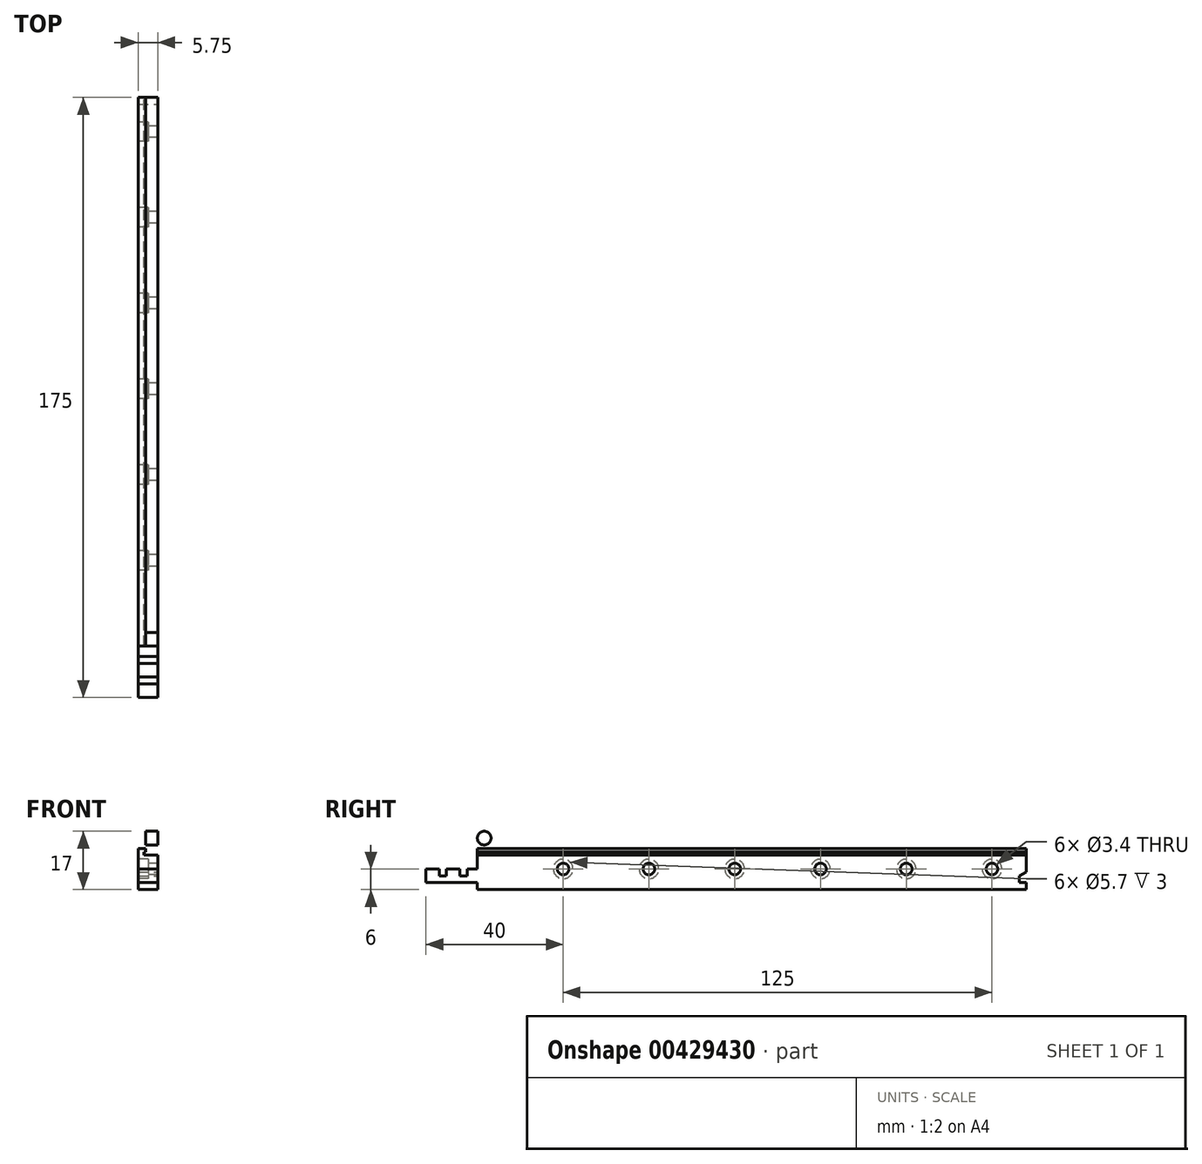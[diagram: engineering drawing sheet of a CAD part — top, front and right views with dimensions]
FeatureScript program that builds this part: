
annotation { "Feature Type Name" : "Feature", "Feature Type Description" : "" }
export const myFeature = defineFeature(function(context is Context, id is Id, definition is map)
    precondition{}
    {
        {
            var Q0;
            Q0=qCreatedBy(makeId("Right.planeOp"),FACE);
            var sketch = newSketch(context, id + "F0", { "sketchPlane" : qUnion([Q0])});
            skLineSegment(sketch, "E0.bottom", {"start": v(-160, 10) * mm, "end": v(0, 10) * mm});
            skLineSegment(sketch, "E0.top", {"start": v(-160, 0) * mm, "end": v(0, 0) * mm});
            skLineSegment(sketch, "E0.left", {"start": v(-160, 10) * mm, "end": v(-160, 0) * mm});
            skLineSegment(sketch, "E0.right", {"start": v(0, 10) * mm, "end": v(0, 0) * mm});
            skLineSegment(sketch, "E1.bottom", {"start": v(-160, 10) * mm, "end": v(-156, 10) * mm});
            skLineSegment(sketch, "E1.top", {"start": v(-158, 15) * mm, "end": v(-158, 15) * mm});
            skLineSegment(sketch, "E1.left", {"start": v(-160, 10) * mm, "end": v(-160, 13) * mm});
            skLineSegment(sketch, "E1.right", {"start": v(-156, 10) * mm, "end": v(-156, 13) * mm});
            skPoint(sketch, "E2.visualSharp", {"position": v(-160, 15) * mm});
            skArc(sketch, "E2.filletArc", {"start": v(-158, 15) * mm, "mid": v(-159.41, 14.41) * mm, "end": v(-160, 13) * mm});
            skPoint(sketch, "E3.visualSharp", {"position": v(-156, 15) * mm});
            skArc(sketch, "E3.filletArc", {"start": v(-156, 13) * mm, "mid": v(-156.59, 14.41) * mm, "end": v(-158, 15) * mm});
            skSolve(sketch);
        }
        {
            var Q0;
            Q0=makeQuery(id+"F0.imprint","IMPRINT",FACE,{"disambiguationData":[TD([[makeQuery(id+"F0.imprint","IMPRINT",EDGE,{"derivedFrom":sQuery(id+"F0.wireOp",EDGE,"E0.bottom")}),-1.0]])]});
            var Q1;
            Q1=makeQuery(id+"F0.imprint","IMPRINT",FACE,{"disambiguationData":[TD([[makeQuery(id+"F0.imprint","IMPRINT",EDGE,{"derivedFrom":sQuery(id+"F0.wireOp",EDGE,"E1.bottom")}),1.0]])]});
            extrude(context, id + "F1", {"entities" : qUnion([Q0, Q1]), "depth" : 5.75 * mm});
        }
        {
            var Q0;
            Q0=makeQuery(id+"F1.opExtrude","CAP_FACE",FACE,{"disambiguationData":[OSD([sQuery(id+"F0.wireOp",EDGE,"E0.bottom"),sQuery(id+"F0.wireOp",EDGE,"E0.top"),sQuery(id+"F0.wireOp",EDGE,"E0.left"),sQuery(id+"F0.wireOp",EDGE,"E0.right")])],"isStart":false});
            var sketch = newSketch(context, id + "F2", { "sketchPlane" : qUnion([Q0])});
            skLineSegment(sketch, "E4.bottom", {"start": v(-160, 9) * mm, "end": v(0, 9) * mm});
            skLineSegment(sketch, "E4.top", {"start": v(-160, 8.1) * mm, "end": v(0, 8.1) * mm});
            skLineSegment(sketch, "E4.left", {"start": v(-160, 9) * mm, "end": v(-160, 8.1) * mm});
            skLineSegment(sketch, "E4.right", {"start": v(0, 9) * mm, "end": v(0, 8.1) * mm});
            skSolve(sketch);
        }
        {
            var Q0;
            Q0=makeQuery(id+"F2.imprint","IMPRINT",FACE,{"disambiguationData":[TD([[makeQuery(id+"F2.imprint","IMPRINT",EDGE,{"derivedFrom":sQuery(id+"F2.wireOp",EDGE,"E4.bottom")}),-1.0]])]});
            extrude(context, id + "F3", {"entities" : qUnion([Q0]), "operationType" : NewBodyOperationType.REMOVE, "oppositeDirection" : true, "depth" : 4.1 * mm});
        }
        {
            var Q0;
            {var subQ0=sQuery(id+"F0.wireOp",EDGE,"E0.bottom");var subQ1=sQuery(id+"F0.wireOp",EDGE,"E0.right");var subQ2=sQuery(id+"F0.wireOp",EDGE,"E0.left");Q0=makeQuery(id+"F3.boolean.opBoolean","SPLIT",FACE,{"disambiguationData":[TD([makeQuery(id+"F1.opExtrude","SWEPT_FACE",FACE,{"disambiguationData":[OSD([subQ0])]})])],"derivedFrom":makeQuery(id+"F1.opExtrude","CAP_FACE",FACE,{"disambiguationData":[OSD([subQ0,sQuery(id+"F0.wireOp",EDGE,"E0.top"),subQ2,subQ1])],"isStart":false})});}
            var sketch = newSketch(context, id + "F4", { "sketchPlane" : qUnion([Q0])});
            skSolve(sketch);
        }
        {
            var Q0;
            Q0 = qSketchRegion(id + "F4", true);
            var Q1;
            {var subQ0=sQuery(id+"F0.wireOp",EDGE,"E0.bottom");Q1=makeQuery(id+"F4.imprint","IMPRINT",FACE,{"disambiguationData":[TD([[makeQuery(id+"F4.imprint","IMPRINT",EDGE,{"derivedFrom":makeQuery(id+"F1.opExtrude","CAP_EDGE",EDGE,{"disambiguationData":[OSD([subQ0])],"isStart":false})}),-1.0]])]});}
            extrude(context, id + "F5", {"entities" : qUnion([Q0, Q1]), "operationType" : NewBodyOperationType.REMOVE, "oppositeDirection" : true, "depth" : 3.5 * mm});
        }
        {
            var Q0;
            Q0=makeQuery(id+"F1.opExtrude","CAP_FACE",FACE,{"disambiguationData":[OSD([sQuery(id+"F0.wireOp",EDGE,"E0.bottom"),sQuery(id+"F0.wireOp",EDGE,"E0.top"),sQuery(id+"F0.wireOp",EDGE,"E0.left"),sQuery(id+"F0.wireOp",EDGE,"E0.right")])],"isStart":true});
            var sketch = newSketch(context, id + "F6", { "sketchPlane" : qUnion([Q0])});
            skLineSegment(sketch, "E5", {"start": v(0, 4) * mm, "end": v(160, 4) * mm, "construction": true});
            skPoint(sketch, "E5.endSnap0", {"position": v(160, 6.5) * mm});
            skCircle(sketch, "E6", {"center": v(135, 4) * mm, "radius": 1.7 * mm});
            skCircle(sketch, "E7", {"center": v(3, 4) * mm, "radius": 1.25 * mm});
            skCircle(sketch, "E8.1.0.0", {"center": v(110, 4) * mm, "radius": 1.7 * mm});
            skCircle(sketch, "E8.2.0.0", {"center": v(85, 4) * mm, "radius": 1.7 * mm});
            skCircle(sketch, "E8.3.0.0", {"center": v(60, 4) * mm, "radius": 1.7 * mm});
            skCircle(sketch, "E8.4.0.0", {"center": v(35, 4) * mm, "radius": 1.7 * mm});
            skCircle(sketch, "E8.5.0.0", {"center": v(10, 4) * mm, "radius": 1.7 * mm});
            skLineSegment(sketch, "E8.direction1", {"start": v(135, 4) * mm, "end": v(110, 4) * mm, "construction": true});
            skSolve(sketch);
        }
        {
            var Q0;
            Q0=makeQuery(id+"F6.imprint","IMPRINT",FACE,{"disambiguationData":[TD([[makeQuery(id+"F6.imprint","IMPRINT",EDGE,{"derivedFrom":sQuery(id+"F6.wireOp",EDGE,"sVQ4iHpu-8XnO-mIip-v3Sc-kH5FdKVcQHpS")}),1.0]])]});
            var Q1;
            Q1=makeQuery(id+"F6.imprint","IMPRINT",FACE,{"disambiguationData":[TD([[makeQuery(id+"F6.imprint","IMPRINT",EDGE,{"derivedFrom":sQuery(id+"F6.wireOp",EDGE,"hsN1ZB3G-UoCD-3FgG-QDpg-hoPAJprMlxeB")}),1.0]])]});
            var Q2;
            Q2=makeQuery(id+"F6.imprint","IMPRINT",FACE,{"disambiguationData":[TD([[makeQuery(id+"F6.imprint","IMPRINT",EDGE,{"derivedFrom":sQuery(id+"F6.wireOp",EDGE,"E6")}),1.0]])]});
            var Q3;
            Q3=makeQuery(id+"F6.imprint","IMPRINT",FACE,{"disambiguationData":[TD([[makeQuery(id+"F6.imprint","IMPRINT",EDGE,{"derivedFrom":sQuery(id+"F6.wireOp",EDGE,"E8.1.0.0")}),1.0]])]});
            var Q4;
            Q4=makeQuery(id+"F6.imprint","IMPRINT",FACE,{"disambiguationData":[TD([[makeQuery(id+"F6.imprint","IMPRINT",EDGE,{"derivedFrom":sQuery(id+"F6.wireOp",EDGE,"E8.2.0.0")}),1.0]])]});
            var Q5;
            Q5=makeQuery(id+"F6.imprint","IMPRINT",FACE,{"disambiguationData":[TD([[makeQuery(id+"F6.imprint","IMPRINT",EDGE,{"derivedFrom":sQuery(id+"F6.wireOp",EDGE,"E8.3.0.0")}),1.0]])]});
            var Q6;
            Q6=makeQuery(id+"F6.imprint","IMPRINT",FACE,{"disambiguationData":[TD([[makeQuery(id+"F6.imprint","IMPRINT",EDGE,{"derivedFrom":sQuery(id+"F6.wireOp",EDGE,"E8.4.0.0")}),1.0]])]});
            var Q7;
            Q7=makeQuery(id+"F6.imprint","IMPRINT",FACE,{"disambiguationData":[TD([[makeQuery(id+"F6.imprint","IMPRINT",EDGE,{"derivedFrom":sQuery(id+"F6.wireOp",EDGE,"E8.5.0.0")}),1.0]])]});
            extrude(context, id + "F7", {"entities" : qUnion([Q0, Q1, Q2, Q3, Q4, Q5, Q6, Q7]), "operationType" : NewBodyOperationType.REMOVE, "oppositeDirection" : true, "depth" : 25 * mm});
        }
        {
            var Q0;
            Q0=makeQuery(id+"F1.opExtrude","CAP_FACE",FACE,{"disambiguationData":[OSD([sQuery(id+"F0.wireOp",EDGE,"E0.bottom"),sQuery(id+"F0.wireOp",EDGE,"E0.top"),sQuery(id+"F0.wireOp",EDGE,"E0.left"),sQuery(id+"F0.wireOp",EDGE,"E0.right")])],"isStart":true});
            var sketch = newSketch(context, id + "F8", { "sketchPlane" : qUnion([Q0])});
            skLineSegment(sketch, "E9.0.0", {"start": v(160, 0) * mm, "end": v(160, 13) * mm});
            skLineSegment(sketch, "E9.0.2", {"start": v(0, 10) * mm, "end": v(0, 0) * mm});
            skLineSegment(sketch, "E9.0.3", {"start": v(0, 0) * mm, "end": v(160, 0) * mm});
            skCircle(sketch, "E10", {"center": v(135, 4) * mm, "radius": 2.85 * mm});
            skCircle(sketch, "E11.1.0.0", {"center": v(110, 4) * mm, "radius": 2.85 * mm});
            skCircle(sketch, "E11.2.0.0", {"center": v(85, 4) * mm, "radius": 2.85 * mm});
            skCircle(sketch, "E11.3.0.0", {"center": v(60, 4) * mm, "radius": 2.85 * mm});
            skCircle(sketch, "E11.4.0.0", {"center": v(35, 4) * mm, "radius": 2.85 * mm});
            skCircle(sketch, "E11.5.0.0", {"center": v(10, 4) * mm, "radius": 2.85 * mm});
            skLineSegment(sketch, "E11.direction1", {"start": v(135, 4) * mm, "end": v(110, 4) * mm, "construction": true});
            skSolve(sketch);
        }
        {
            var Q0;
            Q0=makeQuery(id+"F8.imprint","IMPRINT",FACE,{"disambiguationData":[TD([[makeQuery(id+"F8.imprint","IMPRINT",EDGE,{"derivedFrom":sQuery(id+"F8.wireOp",EDGE,"YmYcqx3s-BiXW-tcQ6-Nhu7-wGdmN5bGpZN7")}),1.0]])]});
            var Q1;
            Q1=makeQuery(id+"F8.imprint","IMPRINT",FACE,{"disambiguationData":[TD([[makeQuery(id+"F8.imprint","IMPRINT",EDGE,{"derivedFrom":sQuery(id+"F8.wireOp",EDGE,"wS4yzpAT-0Ree-8Seg-Sxwu-vB1dnwpMkMpn")}),1.0]])]});
            var Q2;
            Q2=makeQuery(id+"F8.imprint","IMPRINT",FACE,{"disambiguationData":[TD([[makeQuery(id+"F8.imprint","IMPRINT",EDGE,{"derivedFrom":sQuery(id+"F8.wireOp",EDGE,"E10")}),1.0]])]});
            var Q3;
            Q3=makeQuery(id+"F8.imprint","IMPRINT",FACE,{"disambiguationData":[TD([[makeQuery(id+"F8.imprint","IMPRINT",EDGE,{"derivedFrom":sQuery(id+"F8.wireOp",EDGE,"E11.1.0.0")}),1.0]])]});
            var Q4;
            Q4=makeQuery(id+"F8.imprint","IMPRINT",FACE,{"disambiguationData":[TD([[makeQuery(id+"F8.imprint","IMPRINT",EDGE,{"derivedFrom":sQuery(id+"F8.wireOp",EDGE,"E11.2.0.0")}),1.0]])]});
            var Q5;
            Q5=makeQuery(id+"F8.imprint","IMPRINT",FACE,{"disambiguationData":[TD([[makeQuery(id+"F8.imprint","IMPRINT",EDGE,{"derivedFrom":sQuery(id+"F8.wireOp",EDGE,"E11.3.0.0")}),1.0]])]});
            var Q6;
            Q6=makeQuery(id+"F8.imprint","IMPRINT",FACE,{"disambiguationData":[TD([[makeQuery(id+"F8.imprint","IMPRINT",EDGE,{"derivedFrom":sQuery(id+"F8.wireOp",EDGE,"E11.4.0.0")}),1.0]])]});
            var Q7;
            Q7=makeQuery(id+"F8.imprint","IMPRINT",FACE,{"disambiguationData":[TD([[makeQuery(id+"F8.imprint","IMPRINT",EDGE,{"derivedFrom":sQuery(id+"F8.wireOp",EDGE,"E11.5.0.0")}),1.0]])]});
            extrude(context, id + "F9", {"entities" : qUnion([Q0, Q1, Q2, Q3, Q4, Q5, Q6, Q7]), "operationType" : NewBodyOperationType.REMOVE, "oppositeDirection" : true, "depth" : 3 * mm});
        }
        {
            var Q0;
            Q0=makeQuery(id+"F5.boolean.opBoolean","COPY",FACE,{"derivedFrom":makeQuery(id+"F5.opExtrude","CAP_FACE",FACE,{"disambiguationData":[OSD([sQuery(id+"F0.wireOp",EDGE,"E0.bottom"),sQuery(id+"F0.wireOp",EDGE,"E0.left"),sQuery(id+"F0.wireOp",EDGE,"E0.right"),sQuery(id+"F0.wireOp",EDGE,"E1.left"),sQuery(id+"F0.wireOp",EDGE,"E1.right"),sQuery(id+"F0.wireOp",EDGE,"E2.filletArc"),sQuery(id+"F0.wireOp",EDGE,"E3.filletArc"),sQuery(id+"F2.wireOp",EDGE,"E4.bottom")])],"isStart":false})});
            var sketch = newSketch(context, id + "F10", { "sketchPlane" : qUnion([Q0])});
            skArc(sketch, "E12.0", {"start": v(-156, 13) * mm, "mid": v(-158, 15) * mm, "end": v(-160, 13) * mm});
            skCircle(sketch, "E13", {"center": v(-158, 13) * mm, "radius": 2 * mm});
            skSolve(sketch);
        }
        {
            var Q0;
            {var subQ0=sQuery(id+"F10.wireOp",EDGE,"E13");var subQ2=makeQuery(id+"F10.imprint","INTERSECT",VERTEX,{"derivedFrom":[makeQuery(id+"F5.boolean.opBoolean","COPY",EDGE,{"derivedFrom":makeQuery(id+"F5.opExtrude","CAP_EDGE",EDGE,{"disambiguationData":[OSD([sQuery(id+"F0.wireOp",EDGE,"E1.right")])],"isStart":false})}),subQ0]});Q0=makeQuery(id+"F10.imprint","IMPRINT",FACE,{"disambiguationData":[TD([[makeQuery(id+"F10.imprint","IMPRINT",EDGE,{"disambiguationData":[TD([[subQ2,-1.0]])],"derivedFrom":subQ0}),1.0]])]});}
            var Q1;
            {var subQ0=sQuery(id+"F0.wireOp",EDGE,"E0.top");var subQ1=sQuery(id+"F0.wireOp",EDGE,"E1.left");var subQ2=sQuery(id+"F0.wireOp",EDGE,"E0.left");var subQ3=sQuery(id+"F0.wireOp",EDGE,"E0.right");Q1=makeQuery(id+"F3.boolean.opBoolean","SPLIT",FACE,{"disambiguationData":[TD([makeQuery(id+"F1.opExtrude","SWEPT_FACE",FACE,{"disambiguationData":[OSD([subQ0])]})])],"derivedFrom":makeQuery(id+"F1.opExtrude","CAP_FACE",FACE,{"disambiguationData":[OSD([sQuery(id+"F0.wireOp",EDGE,"E0.bottom"),subQ0,subQ2,subQ3,subQ1,sQuery(id+"F0.wireOp",EDGE,"E1.right"),sQuery(id+"F0.wireOp",EDGE,"E2.filletArc"),sQuery(id+"F0.wireOp",EDGE,"E3.filletArc")])],"isStart":false})});}
            extrude(context, id + "F11", {"entities" : qUnion([Q0]), "operationType" : NewBodyOperationType.ADD, "endBound" : BoundingType.UP_TO_SURFACE, "endBoundEntityFace" : qUnion([Q1]), "depth" : 25 * mm});
        }
        {
            var Q0;
            Q0=makeQuery(id+"F1.opExtrude","SWEPT_FACE",FACE,{"disambiguationData":[OSD([sQuery(id+"F0.wireOp",EDGE,"E0.top")])]});
            var sketch = newSketch(context, id + "F12", { "sketchPlane" : qUnion([Q0])});
            skLineSegment(sketch, "E14.bottom", {"start": v(0, 160) * mm, "end": v(2, 160) * mm});
            skLineSegment(sketch, "E14.top", {"start": v(0, 0) * mm, "end": v(2, 0) * mm});
            skLineSegment(sketch, "E14.left", {"start": v(0, 160) * mm, "end": v(0, 0) * mm});
            skLineSegment(sketch, "E14.right", {"start": v(2, 160) * mm, "end": v(2, 0) * mm});
            skSolve(sketch);
        }
        {
            var Q0;
            Q0=makeQuery(id+"F12.imprint","IMPRINT",FACE,{"disambiguationData":[TD([[makeQuery(id+"F12.imprint","IMPRINT",EDGE,{"derivedFrom":sQuery(id+"F12.wireOp",EDGE,"E14.bottom")}),1.0]])]});
            var Q1;
            {var subQ0=sQuery(id+"F12.wireOp",EDGE,"E14.right");Q1=makeQuery(id+"F12.imprint","IMPRINT",FACE,{"disambiguationData":[TD([[makeQuery(id+"F12.imprint","IMPRINT",EDGE,{"derivedFrom":subQ0}),1.0]])]});}
            extrude(context, id + "F13", {"entities" : qUnion([Q0, Q1]), "operationType" : NewBodyOperationType.ADD, "depth" : 2 * mm});
        }
        {
            var Q0;
            {var subQ0=sQuery(id+"F0.wireOp",EDGE,"E0.top");var subQ1=sQuery(id+"F0.wireOp",EDGE,"E1.left");var subQ2=sQuery(id+"F0.wireOp",EDGE,"E0.left");var subQ3=sQuery(id+"F0.wireOp",EDGE,"E0.right");Q0=makeQuery(id+"F3.boolean.opBoolean","SPLIT",FACE,{"disambiguationData":[TD([makeQuery(id+"F1.opExtrude","SWEPT_FACE",FACE,{"disambiguationData":[OSD([subQ0])]})])],"derivedFrom":makeQuery(id+"F1.opExtrude","CAP_FACE",FACE,{"disambiguationData":[OSD([sQuery(id+"F0.wireOp",EDGE,"E0.bottom"),subQ0,subQ2,subQ3,subQ1,sQuery(id+"F0.wireOp",EDGE,"E1.right"),sQuery(id+"F0.wireOp",EDGE,"E2.filletArc"),sQuery(id+"F0.wireOp",EDGE,"E3.filletArc")])],"isStart":false})});}
            var sketch = newSketch(context, id + "F14", { "sketchPlane" : qUnion([Q0])});
            skLineSegment(sketch, "E15.bottom", {"start": v(-160, 0) * mm, "end": v(-175, 0) * mm});
            skLineSegment(sketch, "E15.top", {"start": v(-160, 4) * mm, "end": v(-175, 4) * mm});
            skLineSegment(sketch, "E15.left", {"start": v(-160, 0) * mm, "end": v(-160, 4) * mm});
            skLineSegment(sketch, "E15.right", {"start": v(-175, 0) * mm, "end": v(-175, 4) * mm});
            skLineSegment(sketch, "E16.bottom", {"start": v(-171.1, 4) * mm, "end": v(-169, 4) * mm});
            skLineSegment(sketch, "E16.top", {"start": v(-171.1, 1.9) * mm, "end": v(-169, 1.9) * mm});
            skLineSegment(sketch, "E16.left", {"start": v(-171.1, 4) * mm, "end": v(-171.1, 1.9) * mm});
            skLineSegment(sketch, "E16.right", {"start": v(-169, 4) * mm, "end": v(-169, 1.9) * mm});
            skLineSegment(sketch, "E17.bottom", {"start": v(-165.1, 4) * mm, "end": v(-163, 4) * mm});
            skLineSegment(sketch, "E17.top", {"start": v(-165.1, 1.9) * mm, "end": v(-163, 1.9) * mm});
            skLineSegment(sketch, "E17.left", {"start": v(-165.1, 4) * mm, "end": v(-165.1, 1.9) * mm});
            skLineSegment(sketch, "E17.right", {"start": v(-163, 4) * mm, "end": v(-163, 1.9) * mm});
            skSolve(sketch);
        }
        {
            var Q0;
            Q0=makeQuery(id+"F14.imprint","IMPRINT",FACE,{"disambiguationData":[TD([[makeQuery(id+"F14.imprint","IMPRINT",EDGE,{"derivedFrom":sQuery(id+"F14.wireOp",EDGE,"LsfhYElW-W3LQ-IoJA-5lva-SZOnABNH6nI7.bottom")}),-1.0]])]});
            var Q1;
            Q1=makeQuery(id+"F14.imprint","IMPRINT",FACE,{"disambiguationData":[TD([[makeQuery(id+"F14.imprint","IMPRINT",EDGE,{"derivedFrom":sQuery(id+"F14.wireOp",EDGE,"E15.bottom")}),-1.0]])]});
            var Q2;
            Q2=makeQuery(id+"F13.boolean.opBoolean","MERGE",FACE,{"derivedFrom":[makeQuery(id+"F1.opExtrude","CAP_FACE",FACE,{"disambiguationData":[OSD([sQuery(id+"F0.wireOp",EDGE,"E0.bottom"),sQuery(id+"F0.wireOp",EDGE,"E0.top"),sQuery(id+"F0.wireOp",EDGE,"E0.left"),sQuery(id+"F0.wireOp",EDGE,"E0.right"),sQuery(id+"F0.wireOp",EDGE,"E1.left"),sQuery(id+"F0.wireOp",EDGE,"E1.right"),sQuery(id+"F0.wireOp",EDGE,"E2.filletArc"),sQuery(id+"F0.wireOp",EDGE,"E3.filletArc")])],"isStart":true}),makeQuery(id+"F13.opExtrude","SWEPT_FACE",FACE,{"disambiguationData":[OSD([sQuery(id+"F12.wireOp",EDGE,"E14.left")])]})]});
            extrude(context, id + "F15", {"entities" : qUnion([Q0, Q1]), "operationType" : NewBodyOperationType.ADD, "endBound" : BoundingType.UP_TO_SURFACE, "oppositeDirection" : true, "endBoundEntityFace" : qUnion([Q2]), "depth" : 3 * mm});
        }
        {
            var Q0;
            {var subQ0=sQuery(id+"F0.wireOp",EDGE,"E0.top");var subQ1=sQuery(id+"F0.wireOp",EDGE,"E1.left");var subQ2=sQuery(id+"F0.wireOp",EDGE,"E0.left");var subQ3=sQuery(id+"F0.wireOp",EDGE,"E0.right");Q0=makeQuery(id+"F15.boolean.opBoolean","MERGE",FACE,{"derivedFrom":[makeQuery(id+"F13.boolean.opBoolean","MERGE",FACE,{"derivedFrom":[makeQuery(id+"F3.boolean.opBoolean","SPLIT",FACE,{"disambiguationData":[TD([makeQuery(id+"F1.opExtrude","SWEPT_FACE",FACE,{"disambiguationData":[OSD([subQ0])]})])],"derivedFrom":makeQuery(id+"F1.opExtrude","CAP_FACE",FACE,{"disambiguationData":[OSD([sQuery(id+"F0.wireOp",EDGE,"E0.bottom"),subQ0,subQ2,subQ3,subQ1,sQuery(id+"F0.wireOp",EDGE,"E1.right"),sQuery(id+"F0.wireOp",EDGE,"E2.filletArc"),sQuery(id+"F0.wireOp",EDGE,"E3.filletArc")])],"isStart":false})}),makeQuery(id+"F13.opExtrude","SWEPT_FACE",FACE,{"disambiguationData":[OSD([subQ0])]})]}),makeQuery(id+"F15.opExtrude","CAP_FACE",FACE,{"disambiguationData":[OSD([sQuery(id+"F14.wireOp",EDGE,"E15.bottom"),sQuery(id+"F14.wireOp",EDGE,"E15.top"),sQuery(id+"F14.wireOp",EDGE,"E15.left"),sQuery(id+"F14.wireOp",EDGE,"E15.right"),sQuery(id+"F14.wireOp",EDGE,"E16.top"),sQuery(id+"F14.wireOp",EDGE,"E16.left"),sQuery(id+"F14.wireOp",EDGE,"E16.right"),sQuery(id+"F14.wireOp",EDGE,"E17.top"),sQuery(id+"F14.wireOp",EDGE,"E17.left"),sQuery(id+"F14.wireOp",EDGE,"E17.right")])],"isStart":true})]});}
            var sketch = newSketch(context, id + "F16", { "sketchPlane" : qUnion([Q0])});
            skLineSegment(sketch, "E18", {"start": v(0, 0) * mm, "end": v(-2, 0) * mm});
            skLineSegment(sketch, "E19", {"start": v(-2, 0) * mm, "end": v(-2, 2) * mm});
            skLineSegment(sketch, "E20", {"start": v(-2, 2) * mm, "end": v(0, 3.15) * mm});
            skSolve(sketch);
        }
        {
            var Q0;
            {var subQ0=sQuery(id+"F16.wireOp",EDGE,"E18");Q0=makeQuery(id+"F16.imprint","IMPRINT",FACE,{"disambiguationData":[TD([[makeQuery(id+"F16.imprint","IMPRINT",EDGE,{"derivedFrom":subQ0}),-1.0]])]});}
            extrude(context, id + "F17", {"entities" : qUnion([Q0]), "operationType" : NewBodyOperationType.REMOVE, "oppositeDirection" : true, "depth" : 25 * mm});
        }
    });
